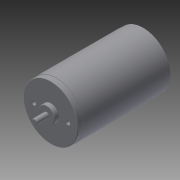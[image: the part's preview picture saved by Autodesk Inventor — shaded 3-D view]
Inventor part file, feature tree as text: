
AUTODESK INVENTOR PART (.ipt)
format: ipt  version: 2014 (Build 180170000, 170)  size: 146,432 bytes
history: native  units: in
note: dims shown in document units (in); Inventor stores cm internally (conversion verified against a paired STEP export)
features: chamfer x1, other x1, imported_body x1
ambient origin geometry x8: Origin, YZ Plane, XZ Plane, XY Plane, X Axis, Y Axis, Z Axis, Center Point
bodies: Body1 (feature_tree)
feature tree (3):
  chamfer  "Chamfer1"  [1 undecoded]
  other  "217-3351-STEP1"
  imported_body  "Base1"
note: 1 required parameter value undecoded (feature->parameter linkage not recoverable at this tier; creation-order binding heuristic only, values carry confidence <= 0.55)
